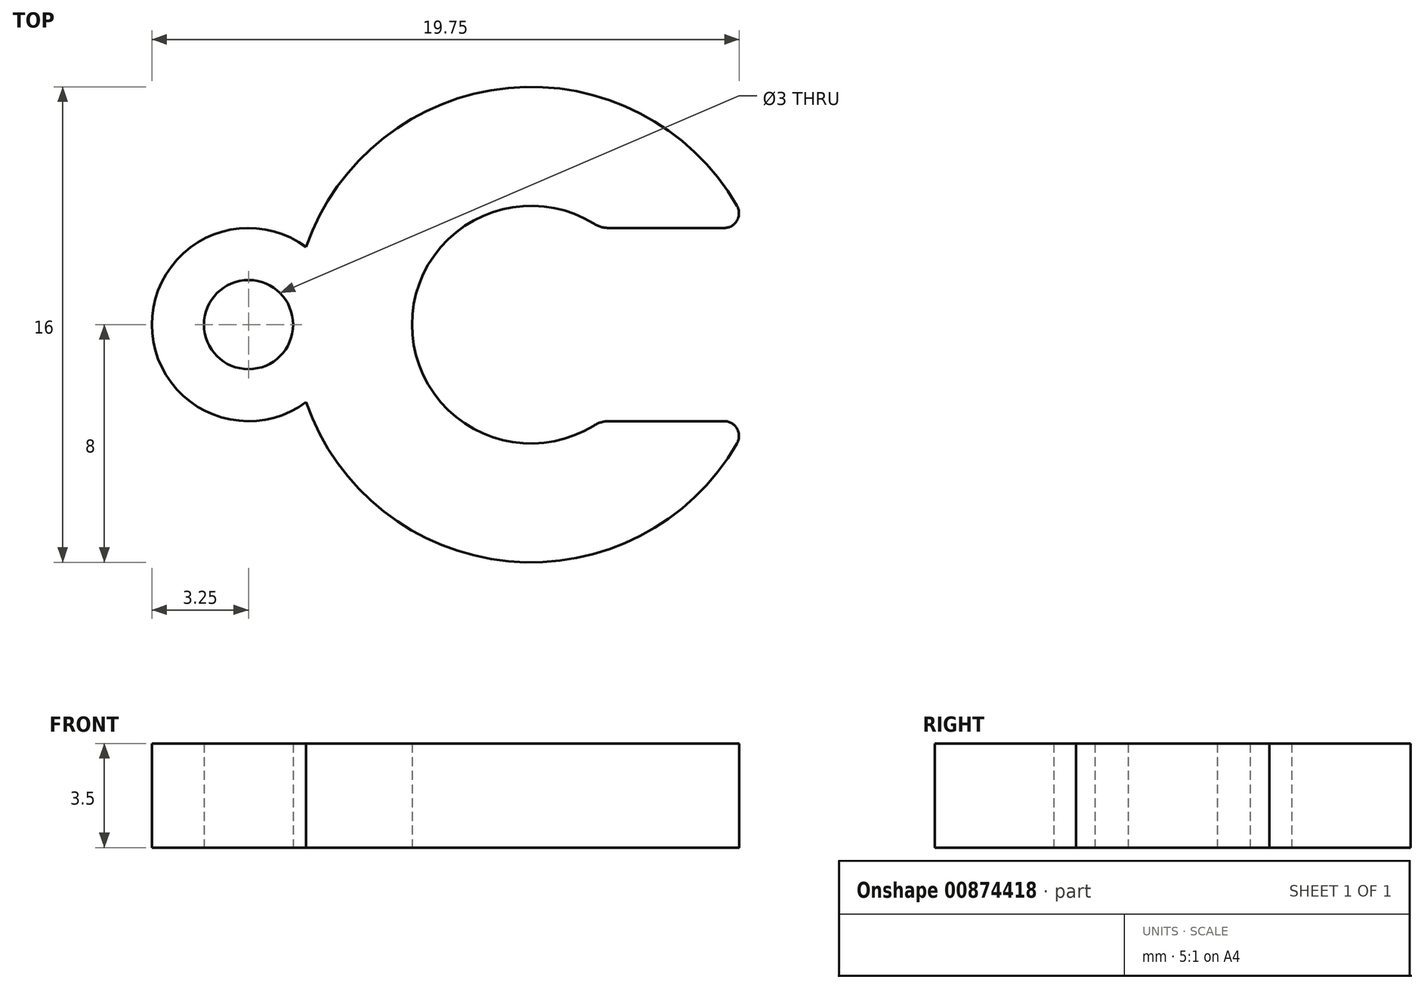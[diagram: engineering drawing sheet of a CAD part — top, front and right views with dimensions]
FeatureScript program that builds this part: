
annotation { "Feature Type Name" : "Feature", "Feature Type Description" : "" }
export const myFeature = defineFeature(function(context is Context, id is Id, definition is map)
    precondition{}
    {
        {
            var Q0;
            Q0=qCreatedBy(makeId("Top.planeOp"),FACE);
            var sketch = newSketch(context, id + "F0", { "sketchPlane" : qUnion([Q0])});
            skArc(sketch, "E0", {"start": v(2.1, 3.4) * mm, "mid": v(-4, 0) * mm, "end": v(2.1, -3.4) * mm});
            skArc(sketch, "E1", {"start": v(6.93, 4) * mm, "mid": v(-0.76, 7.96) * mm, "end": v(-7.56, 2.6) * mm});
            skLineSegment(sketch, "E2.bottom", {"start": v(6.5, 3.25) * mm, "end": v(2.63, 3.25) * mm});
            skLineSegment(sketch, "E2.top", {"start": v(6.5, -3.25) * mm, "end": v(2.63, -3.25) * mm});
            skPoint(sketch, "E3.visualSharp", {"position": v(7.31, 3.25) * mm});
            skArc(sketch, "E3.filletArc", {"start": v(6.5, 3.25) * mm, "mid": v(6.93, 3.5) * mm, "end": v(6.93, 4) * mm});
            skPoint(sketch, "E4.visualSharp", {"position": v(7.31, -3.25) * mm});
            skArc(sketch, "E4.filletArc", {"start": v(6.93, -4) * mm, "mid": v(6.93, -3.5) * mm, "end": v(6.5, -3.25) * mm});
            skPoint(sketch, "E5.visualSharp", {"position": v(2.33, 3.25) * mm});
            skArc(sketch, "E5.filletArc", {"start": v(2.1, 3.4) * mm, "mid": v(2.36, 3.29) * mm, "end": v(2.63, 3.25) * mm});
            skPoint(sketch, "E6.visualSharp", {"position": v(2.33, -3.25) * mm});
            skArc(sketch, "E6.filletArc", {"start": v(2.63, -3.25) * mm, "mid": v(2.36, -3.29) * mm, "end": v(2.1, -3.4) * mm});
            skCircle(sketch, "E7", {"center": v(-9.5, 0) * mm, "radius": 1.5 * mm});
            skPoint(sketch, "E7.centerSnap0", {"position": v(-8, 0) * mm});
            skArc(sketch, "E8", {"start": v(-7.56, 2.6) * mm, "mid": v(-12.75, 0) * mm, "end": v(-7.56, -2.6) * mm});
            skArc(sketch, "E9.trimOffspring", {"start": v(-7.56, -2.6) * mm, "mid": v(-0.76, -7.96) * mm, "end": v(6.93, -4) * mm});
            skSolve(sketch);
        }
        {
            var Q0;
            Q0=makeQuery(id+"F0.imprint","IMPRINT",FACE,{"disambiguationData":[TD([[makeQuery(id+"F0.imprint","IMPRINT",EDGE,{"derivedFrom":sQuery(id+"F0.wireOp",EDGE,"E0")}),-1.0]])]});
            extrude(context, id + "F1", {"entities" : qUnion([Q0]), "depth" : 3.5 * mm, "offsetDistance" : 25 * mm});
        }
    });
